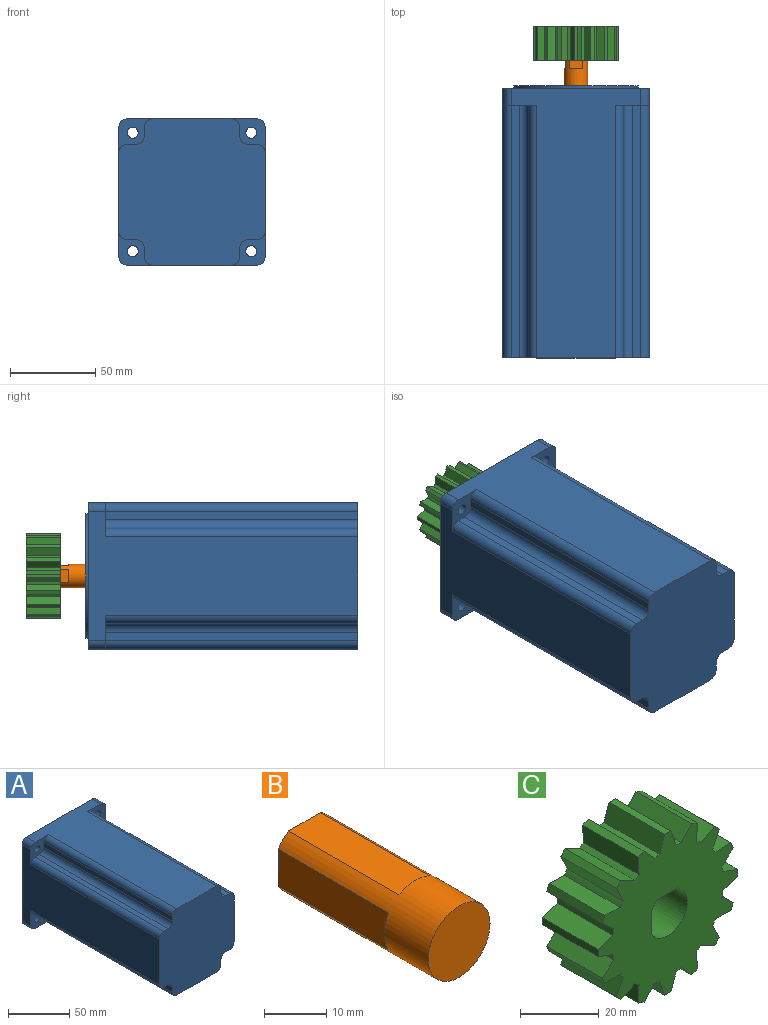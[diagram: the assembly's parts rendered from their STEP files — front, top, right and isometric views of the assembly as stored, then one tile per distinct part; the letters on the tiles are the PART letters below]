
ASSEMBLY  parts=3 mates=2
PART A: 40 faces, bbox 85.8x159.6x85.8 mm
  f0: plane 85.8x85.8mm, normal (0,1,0), area 3022.1mm2, adj f1,f2,f3,f4,f5,f6,f7,f9
  f1: plane 158x75.8mm, normal (1,0,0), area 7536.4mm2, adj f0,f5,f6,f8,f13,f16,f26,f35
  f2: plane 158x75.8mm, normal (0,0,1), area 7536.4mm2, adj f0,f6,f7,f8,f10,f13,f33,f37
  f3: plane 158x75.8mm, normal (-1,0,0), area 7536.4mm2, adj f0,f4,f7,f8,f10,f19,f29,f34
  f4: cylinder r=5mm len=10mm, axis (0,1,0), area 78.5mm2, adj f0,f3,f9,f19
  f5: cylinder r=5mm len=10mm, axis (0,1,0), area 78.5mm2, adj f0,f1,f9,f16
  f6: cylinder r=5mm len=10mm, axis (0,1,0), area 78.5mm2, adj f0,f1,f2,f13
  f7: cylinder r=5mm len=10mm, axis (0,1,0), area 78.5mm2, adj f0,f2,f3,f10
  f8: plane 85.8x85.8mm, normal (0,-1,0), area 6440.2mm2, adj f1,f2,f3,f9,f11,f12,f14,f15
  f9: plane 158x75.8mm, normal (0,0,-1), area 7536.4mm2, adj f0,f4,f5,f8,f16,f19,f27,f31
  f10: plane 20x20mm, normal (0,-1,0), area 191.8mm2, adj f2,f3,f7,f11,f12,f25,f32,f33
  f11: plane 148x5mm, normal (0,0,1), area 740mm2, adj f8,f10,f32,f34
  f12: plane 148x5mm, normal (-1,0,0), area 740mm2, adj f8,f10,f32,f33
  f13: plane 20x20mm, normal (0,-1,0), area 191.8mm2, adj f1,f2,f6,f14,f15,f24,f35,f36
  f14: plane 148x5mm, normal (1,0,0), area 740mm2, adj f8,f13,f36,f37
  f15: plane 148x5mm, normal (0,0,1), area 740mm2, adj f8,f13,f35,f36
  f16: plane 20x20mm, normal (0,-1,0), area 191.8mm2, adj f1,f5,f9,f17,f18,f23,f26,f27
  f17: plane 148x5mm, normal (0,0,-1), area 740mm2, adj f8,f16,f26,f28
  f18: plane 148x5mm, normal (1,0,0), area 740mm2, adj f8,f16,f27,f28
  f19: plane 20x20mm, normal (0,-1,0), area 191.8mm2, adj f3,f4,f9,f20,f21,f22,f29,f30
  f20: plane 148x5mm, normal (-1,0,0), area 740mm2, adj f8,f19,f30,f31
  f21: plane 148x5mm, normal (0,0,-1), area 740mm2, adj f8,f19,f29,f30
  f22: cylinder r=3.25mm len=10mm, axis (0,1,0), area 204.2mm2, adj f0,f19
  f23: cylinder r=3.25mm len=10mm, axis (0,1,0), area 204.2mm2, adj f0,f16
  f24: cylinder r=3.25mm len=10mm, axis (0,1,0), area 204.2mm2, adj f0,f13
  f25: cylinder r=3.25mm len=10mm, axis (0,1,0), area 204.2mm2, adj f0,f10
  f26: cylinder r=5mm len=148mm, axis (0,-1,0), area 1162.4mm2, adj f1,f8,f16,f17
  f27: cylinder r=5mm len=148mm, axis (0,1,0), area 1162.4mm2, adj f8,f9,f16,f18
  f28: cylinder r=5mm len=148mm, axis (0,1,0), area 1162.4mm2, adj f8,f16,f17,f18
  f29: cylinder r=5mm len=148mm, axis (0,-1,0), area 1162.4mm2, adj f3,f8,f19,f21
  f30: cylinder r=5mm len=148mm, axis (0,1,0), area 1162.4mm2, adj f8,f19,f20,f21
  f31: cylinder r=5mm len=148mm, axis (0,-1,0), area 1162.4mm2, adj f8,f9,f19,f20
  f32: cylinder r=5mm len=148mm, axis (0,1,0), area 1162.4mm2, adj f8,f10,f11,f12
  f33: cylinder r=5mm len=148mm, axis (0,-1,0), area 1162.4mm2, adj f2,f8,f10,f12
  f34: cylinder r=5mm len=148mm, axis (0,1,0), area 1162.4mm2, adj f3,f8,f10,f11
  f35: cylinder r=5mm len=148mm, axis (0,1,0), area 1162.4mm2, adj f1,f8,f13,f15
  f36: cylinder r=5mm len=148mm, axis (0,1,0), area 1162.4mm2, adj f8,f13,f14,f15
  f37: cylinder r=5mm len=148mm, axis (0,1,0), area 1162.4mm2, adj f2,f8,f13,f14
  f38: cylinder r=36.5mm len=73mm, axis (0,-1,0), area 366.9mm2, adj f0,f39
  f39: plane 73x73mm, normal (0,1,0), area 4185.4mm2, adj f38
PART B: 7 faces, bbox 14x35x14 mm
  f0: cylinder r=7mm len=35mm, axis (0,-1,0), area 1160.6mm2, adj f1,f2,f3,f4,f5,f6
  f1: plane 13x13mm, normal (0,1,0), area 144.2mm2, adj f0,f4,f6
  f2: plane 14x14mm, normal (0,-1,0), area 153.9mm2, adj f0
  f3: plane 7.21x1mm, normal (0,1,0), area 4.9mm2, adj f0,f4
  f4: plane 25x7.21mm, normal (0,0,1), area 180.3mm2, adj f0,f1,f3
  f5: plane 7.21x1mm, normal (0,1,0), area 4.9mm2, adj f0,f6
  f6: plane 25x7.21mm, normal (-1,0,0), area 180.3mm2, adj f0,f1,f5
PART C: 70 faces, bbox 50x20x50 mm
  f0: plane 20x5.56mm, normal (-0.04,0,1), area 111.2mm2, adj f1,f63,f64,f65
  f1: cylinder r=20mm len=20mm, axis (0,1,0), area 36.6mm2, adj f0,f2,f64,f65
  f2: plane 20x5.04mm, normal (0.91,0,-0.42), area 111.2mm2, adj f1,f3,f64,f65
  f3: plane 20x1.55mm, normal (0.71,0,0.71), area 43.9mm2, adj f2,f4,f64,f65
  f4: plane 20x5.04mm, normal (-0.42,0,0.91), area 111.2mm2, adj f3,f5,f64,f65
  f5: cylinder r=20mm len=20mm, axis (0,1,0), area 36.6mm2, adj f4,f6,f64,f65
  f6: plane 20x5.56mm, normal (1,0,-0.04), area 111.2mm2, adj f5,f7,f64,f65
  f7: plane 20x2.03mm, normal (0.38,0,0.92), area 43.9mm2, adj f6,f8,f64,f65
  f8: plane 20x4.1mm, normal (-0.74,0,0.68), area 111.2mm2, adj f7,f9,f64,f65
  f9: cylinder r=20mm len=20mm, axis (0,1,0), area 36.6mm2, adj f8,f10,f64,f65
  f10: plane 20x5.23mm, normal (0.94,0,0.34), area 111.2mm2, adj f9,f11,f64,f65
  f11: plane 20x2.2mm, normal (0,0,1), area 43.9mm2, adj f10,f12,f64,f65
  f12: plane 20x5.23mm, normal (-0.94,0,0.34), area 111.2mm2, adj f11,f13,f64,f65
  f13: cylinder r=20mm len=20mm, axis (0,1,0), area 36.6mm2, adj f12,f14,f64,f65
  f14: plane 20x4.1mm, normal (0.74,0,0.68), area 111.2mm2, adj f13,f15,f64,f65
  f15: plane 20x2.03mm, normal (-0.38,0,0.92), area 43.9mm2, adj f14,f16,f64,f65
  f16: plane 20x5.56mm, normal (-1,0,-0.04), area 111.2mm2, adj f15,f17,f64,f65
  f17: cylinder r=20mm len=20mm, axis (0,1,0), area 36.6mm2, adj f16,f18,f64,f65
  f18: plane 20x5.04mm, normal (0.42,0,0.91), area 111.2mm2, adj f17,f19,f64,f65
  f19: plane 20x1.55mm, normal (-0.71,0,0.71), area 43.9mm2, adj f18,f20,f64,f65
  f20: plane 20x5.04mm, normal (-0.91,0,-0.42), area 111.2mm2, adj f19,f21,f64,f65
  f21: cylinder r=20mm len=20mm, axis (0,1,0), area 36.6mm2, adj f20,f22,f64,f65
  f22: plane 20x5.56mm, normal (0.04,0,1), area 111.2mm2, adj f21,f23,f64,f65
  f23: plane 20x2.03mm, normal (-0.92,0,0.38), area 43.9mm2, adj f22,f24,f64,f65
  f24: plane 20x4.1mm, normal (-0.68,0,-0.74), area 111.2mm2, adj f23,f25,f64,f65
  f25: cylinder r=20mm len=20mm, axis (0,1,0), area 36.6mm2, adj f24,f26,f64,f65
  f26: plane 20x5.23mm, normal (-0.34,0,0.94), area 111.2mm2, adj f25,f27,f64,f65
  f27: plane 20x2.2mm, normal (-1,0,0), area 43.9mm2, adj f26,f28,f64,f65
  f28: plane 20x5.23mm, normal (-0.34,0,-0.94), area 111.2mm2, adj f27,f29,f64,f65
  f29: cylinder r=20mm len=20mm, axis (0,1,0), area 36.6mm2, adj f28,f30,f64,f65
  f30: plane 20x4.1mm, normal (-0.68,0,0.74), area 111.2mm2, adj f29,f31,f64,f65
  f31: plane 20x2.03mm, normal (-0.92,0,-0.38), area 43.9mm2, adj f30,f32,f64,f65
  f32: plane 20x5.56mm, normal (0.04,0,-1), area 111.2mm2, adj f31,f33,f64,f65
  f33: cylinder r=20mm len=20mm, axis (0,1,0), area 36.6mm2, adj f32,f34,f64,f65
  f34: plane 20x5.04mm, normal (-0.91,0,0.42), area 111.2mm2, adj f33,f35,f64,f65
  f35: plane 20x1.55mm, normal (-0.71,0,-0.71), area 43.9mm2, adj f34,f36,f64,f65
  f36: plane 20x5.04mm, normal (0.42,0,-0.91), area 111.2mm2, adj f35,f37,f64,f65
  f37: cylinder r=20mm len=20mm, axis (0,1,0), area 36.6mm2, adj f36,f38,f64,f65
  f38: plane 20x5.56mm, normal (-1,0,0.04), area 111.2mm2, adj f37,f39,f64,f65
  f39: plane 20x2.03mm, normal (-0.38,0,-0.92), area 43.9mm2, adj f38,f40,f64,f65
  f40: plane 20x4.1mm, normal (0.74,0,-0.68), area 111.2mm2, adj f39,f41,f64,f65
  f41: cylinder r=20mm len=20mm, axis (0,1,0), area 36.6mm2, adj f40,f42,f64,f65
  f42: plane 20x5.23mm, normal (-0.94,0,-0.34), area 111.2mm2, adj f41,f43,f64,f65
  f43: plane 20x2.2mm, normal (0,0,-1), area 43.9mm2, adj f42,f44,f64,f65
  f44: plane 20x5.23mm, normal (0.94,0,-0.34), area 111.2mm2, adj f43,f45,f64,f65
  f45: cylinder r=20mm len=20mm, axis (0,1,0), area 36.6mm2, adj f44,f46,f64,f65
  f46: plane 20x4.1mm, normal (-0.74,0,-0.68), area 111.2mm2, adj f45,f47,f64,f65
  f47: plane 20x2.03mm, normal (0.38,0,-0.92), area 43.9mm2, adj f46,f48,f64,f65
  f48: plane 20x5.56mm, normal (1,0,0.04), area 111.2mm2, adj f47,f49,f64,f65
  f49: cylinder r=20mm len=20mm, axis (0,1,0), area 36.6mm2, adj f48,f50,f64,f65
  f50: plane 20x5.04mm, normal (-0.42,0,-0.91), area 111.2mm2, adj f49,f51,f64,f65
  f51: plane 20x1.55mm, normal (0.71,0,-0.71), area 43.9mm2, adj f50,f52,f64,f65
  f52: plane 20x5.04mm, normal (0.91,0,0.42), area 111.2mm2, adj f51,f53,f64,f65
  f53: cylinder r=20mm len=20mm, axis (0,1,0), area 36.6mm2, adj f52,f54,f64,f65
  f54: plane 20x5.56mm, normal (-0.04,0,-1), area 111.2mm2, adj f53,f55,f64,f65
  f55: plane 20x2.03mm, normal (0.92,0,-0.38), area 43.9mm2, adj f54,f56,f64,f65
  f56: plane 20x4.1mm, normal (0.68,0,0.74), area 111.2mm2, adj f55,f57,f64,f65
  f57: cylinder r=20mm len=20mm, axis (0,1,0), area 36.6mm2, adj f56,f58,f64,f65
  f58: plane 20x5.23mm, normal (0.34,0,-0.94), area 111.2mm2, adj f57,f59,f64,f65
  f59: plane 20x2.2mm, normal (1,0,0), area 43.9mm2, adj f58,f60,f64,f65
  f60: plane 20x5.23mm, normal (0.34,0,0.94), area 111.2mm2, adj f59,f61,f64,f65
  f61: cylinder r=20mm len=20mm, axis (0,1,0), area 36.6mm2, adj f60,f62,f64,f65
  f62: plane 20x4.1mm, normal (0.68,0,-0.74), area 111.2mm2, adj f61,f63,f64,f65
  f63: plane 20x2.03mm, normal (0.92,0,0.38), area 43.9mm2, adj f0,f62,f64,f65
  f64: plane 50x50mm, normal (0,-1,0), area 1440.6mm2, adj f0,f1,f2,f3,f4,f5,f6,f7
  f65: plane 50x50mm, normal (0,1,0), area 1440.6mm2, adj f0,f1,f2,f3,f4,f5,f6,f7
  f66: plane 20x7.21mm, normal (1,0,0), area 144.2mm2, adj f64,f65,f67,f69
  f67: cylinder r=7mm len=20mm, axis (0,1,0), area 68.4mm2, adj f64,f65,f66,f68
  f68: plane 20x7.21mm, normal (0,0,-1), area 144.2mm2, adj f64,f65,f67,f69
  f69: cylinder r=7mm len=20mm, axis (0,1,0), area 508.2mm2, adj f64,f65,f66,f68
PLACE A t=(10.35,98.85,-93.03)mm fixed
PLACE B t=(10.35,100.45,-93.03)mm
PLACE C rot(axis=(0,1,0),0deg) t=(10.35,135.45,-93.03)mm
MATE revolute B.f0 <-> A.f38  axis (0,-1,0) through (10.35,100.45,-93.03)mm
MATE fastened B.f0 <-> C.f1  axis (0,1,0) through (10.35,135.45,-93.03)mm
